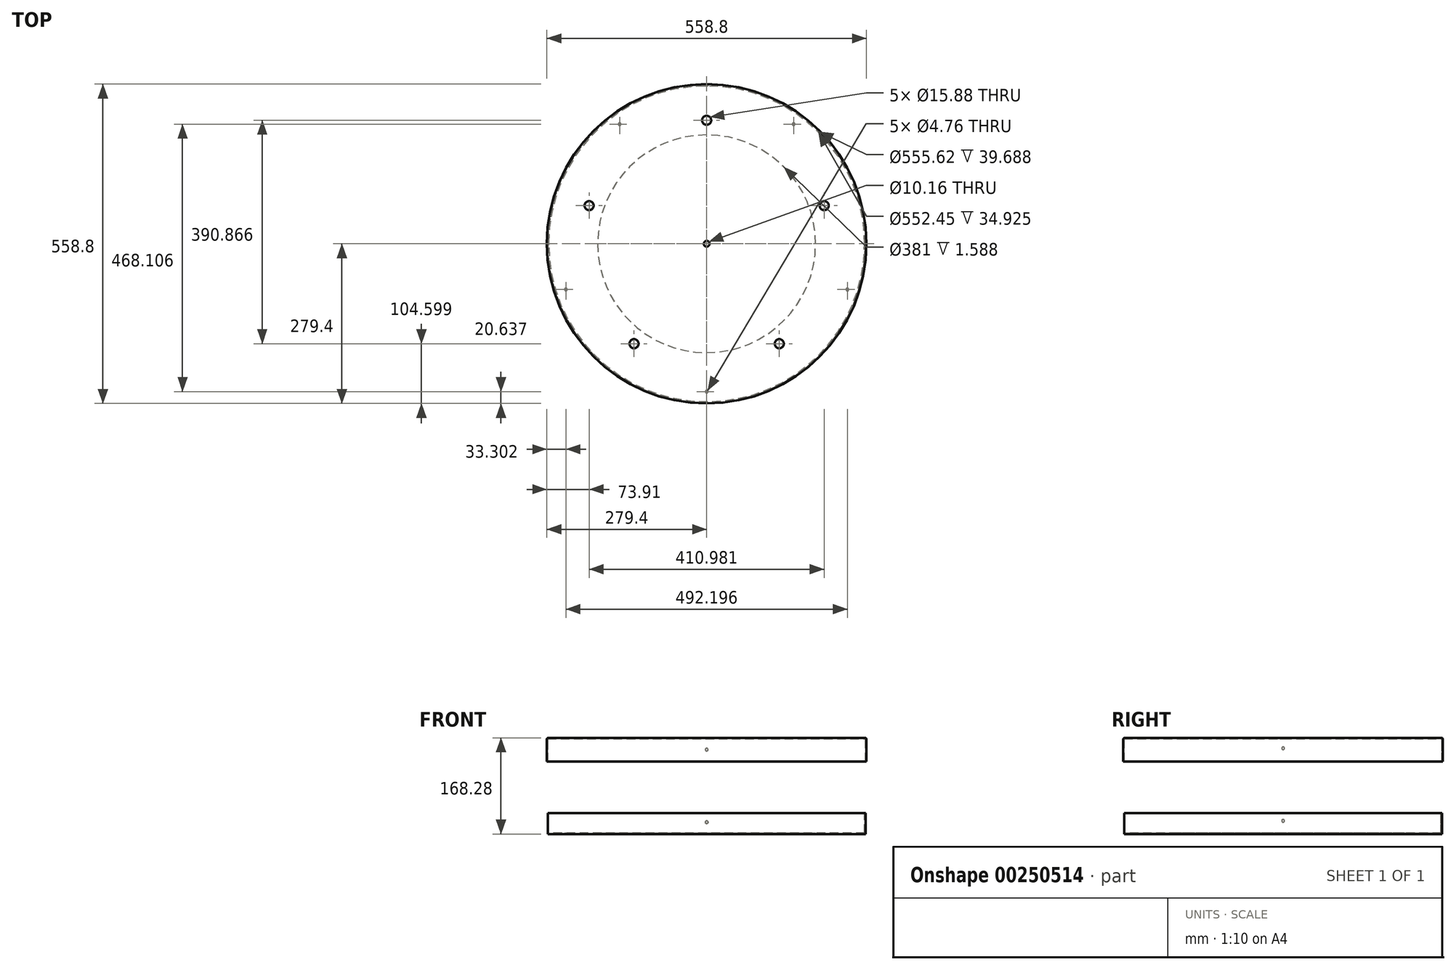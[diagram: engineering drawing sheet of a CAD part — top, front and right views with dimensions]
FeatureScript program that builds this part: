
annotation { "Feature Type Name" : "Feature", "Feature Type Description" : "" }
export const myFeature = defineFeature(function(context is Context, id is Id, definition is map)
    precondition{}
    {
        {
            var Q0;
            Q0=qCreatedBy(makeId("Top.planeOp"),FACE);
            var sketch = newSketch(context, id + "F0", { "sketchPlane" : qUnion([Q0])});
            skCircle(sketch, "E0", {"center": v(0, 0) * mm, "radius": 279.4 * mm});
            skSolve(sketch);
        }
        {
            var Q0;
            Q0 = qSketchRegion(id + "F0", true);
            extrude(context, id + "F1", {"entities" : qUnion([Q0]), "depth" : 1.59 * mm});
        }
        {
            var Q0;
            Q0=makeQuery(id+"F1.opExtrude","CAP_FACE",FACE,{"disambiguationData":[OSD([sQuery(id+"F0.wireOp",EDGE,"E0")])],"isStart":true});
            var sketch = newSketch(context, id + "F2", { "sketchPlane" : qUnion([Q0])});
            skCircle(sketch, "E1.0", {"center": v(0, 0) * mm, "radius": 279.4 * mm});
            skCircle(sketch, "E2.0", {"center": v(0, 0) * mm, "radius": 277.81 * mm});
            skSolve(sketch);
        }
        {
            var Q0;
            Q0 = qSketchRegion(id + "F2", true);
            extrude(context, id + "F3", {"entities" : qUnion([Q0]), "operationType" : NewBodyOperationType.ADD, "depth" : 39.69 * mm});
        }
        {
            var Q0;
            Q0=makeQuery(id+"F1.opExtrude","CAP_FACE",FACE,{"disambiguationData":[OSD([sQuery(id+"F0.wireOp",EDGE,"E0")])],"isStart":false});
            var sketch = newSketch(context, id + "F4", { "sketchPlane" : qUnion([Q0])});
            skCircle(sketch, "E3", {"center": v(0, 216.07) * mm, "radius": 7.94 * mm});
            skCircle(sketch, "E4.1.0", {"center": v(-205.5, 66.77) * mm, "radius": 7.94 * mm});
            skCircle(sketch, "E4.2.0", {"center": v(-127, -174.8) * mm, "radius": 7.94 * mm});
            skCircle(sketch, "E4.3.0", {"center": v(127, -174.8) * mm, "radius": 7.94 * mm});
            skCircle(sketch, "E4.4.0", {"center": v(205.5, 66.77) * mm, "radius": 7.94 * mm});
            skPoint(sketch, "E4.center", {"position": v(0, 0) * mm});
            skCircle(sketch, "E5", {"center": v(0, 0) * mm, "radius": 5.08 * mm});
            skSolve(sketch);
        }
        {
            var Q0;
            Q0 = qSketchRegion(id + "F4", true);
            var Q1;
            Q1=makeQuery(id+"F1.opExtrude","CAP_FACE",FACE,{"disambiguationData":[OSD([sQuery(id+"F0.wireOp",EDGE,"E0")])],"isStart":true});
            extrude(context, id + "F5", {"entities" : qUnion([Q0]), "operationType" : NewBodyOperationType.REMOVE, "endBound" : BoundingType.UP_TO_SURFACE, "oppositeDirection" : true, "endBoundEntityFace" : qUnion([Q1]), "depth" : 25.4 * mm});
        }
        {
            var Q0;
            Q0=makeQuery(id+"F1.opExtrude","CAP_EDGE",EDGE,{"disambiguationData":[OSD([sQuery(id+"F0.wireOp",EDGE,"E0")])],"isStart":false});
            fillet(context, id + "F6", {"entities" : qUnion([Q0]), "radius" : 2.54 * mm, "tangentPropagation" : true, "allowEdgeOverflow" : false});
        }
        {
            var Q0;
            Q0=qCreatedBy(makeId("Front.planeOp"),FACE);
            var sketch = newSketch(context, id + "F7", { "sketchPlane" : qUnion([Q0])});
            skLineSegment(sketch, "E6.0", {"start": v(277.81, 0) * mm, "end": v(-277.81, 0) * mm, "construction": true});
            skLineSegment(sketch, "E6.1", {"start": v(277.81, -39.69) * mm, "end": v(-277.81, -39.69) * mm, "construction": true});
            skLineSegment(sketch, "E7", {"start": v(277.81, -39.69) * mm, "end": v(277.81, -3.18) * mm});
            skLineSegment(sketch, "E8", {"start": v(277.81, -3.18) * mm, "end": v(276.23, -3.18) * mm});
            skLineSegment(sketch, "E9", {"start": v(276.23, -3.18) * mm, "end": v(276.23, -38.1) * mm});
            skLineSegment(sketch, "E10", {"start": v(276.23, -38.1) * mm, "end": v(0, -38.1) * mm});
            skLineSegment(sketch, "E11", {"start": v(0, -38.1) * mm, "end": v(0, -39.69) * mm});
            skLineSegment(sketch, "E12", {"start": v(0, -39.69) * mm, "end": v(277.81, -39.69) * mm});
            skLineSegment(sketch, "E13", {"start": v(0, -39.69) * mm, "end": v(0, -99.27) * mm, "construction": true});
            skSolve(sketch);
        }
        {
            var Q0;
            Q0 = qSketchRegion(id + "F7", true);
            var Q1;
            Q1=sQuery(id+"F7.wireOp",EDGE,"E13");
            revolve(context, id + "F8", {"entities" : qUnion([Q0]), "axis" : qUnion([Q1]), "revolveType" : RevolveType.FULL});
        }
        {
            var Q0;
            Q0=makeQuery(id+"F8.opRevolve","SWEPT_FACE",FACE,{"disambiguationData":[OSD([sQuery(id+"F7.wireOp",EDGE,"E12")])]});
            var sketch = newSketch(context, id + "F9", { "sketchPlane" : qUnion([Q0])});
            skCircle(sketch, "E14", {"center": v(0, 0) * mm, "radius": 190.5 * mm});
            skCircle(sketch, "E15", {"center": v(0, 258.76) * mm, "radius": 2.38 * mm});
            skCircle(sketch, "E16.1.0", {"center": v(-246.1, 79.96) * mm, "radius": 2.38 * mm});
            skCircle(sketch, "E16.2.0", {"center": v(-152.1, -209.34) * mm, "radius": 2.38 * mm});
            skCircle(sketch, "E16.3.0", {"center": v(152.1, -209.34) * mm, "radius": 2.38 * mm});
            skCircle(sketch, "E16.4.0", {"center": v(246.1, 79.96) * mm, "radius": 2.38 * mm});
            skSolve(sketch);
        }
        {
            var Q0;
            Q0 = qSketchRegion(id + "F9", true);
            extrude(context, id + "F10", {"entities" : qUnion([Q0]), "operationType" : NewBodyOperationType.REMOVE, "oppositeDirection" : true, "depth" : 3.17 * mm});
        }
        {
            var Q0;
            Q0=qCreatedBy(makeId("Front.planeOp"),FACE);
            var sketch = newSketch(context, id + "F11", { "sketchPlane" : qUnion([Q0])});
            skLineSegment(sketch, "E17", {"start": v(0, 0) * mm, "end": v(0, -110.02) * mm, "construction": true});
            skSolve(sketch);
        }
        {
            var Q0;
            Q0=qCreatedBy(makeId("Front.planeOp"),FACE);
            var sketch = newSketch(context, id + "F12", { "sketchPlane" : qUnion([Q0])});
            skCircle(sketch, "E18", {"center": v(0, -19.05) * mm, "radius": 2.38 * mm});
            skSolve(sketch);
        }
        {
            var Q0;
            Q0 = qSketchRegion(id + "F12", true);
            extrude(context, id + "F13", {"entities" : qUnion([Q0]), "operationType" : NewBodyOperationType.REMOVE, "endBound" : BoundingType.THROUGH_ALL, "oppositeDirection" : true, "depth" : 25.4 * mm});
        }
        {
            var Q0;
            Q0=qCreatedBy(makeId("Right.planeOp"),FACE);
            var sketch = newSketch(context, id + "F14", { "sketchPlane" : qUnion([Q0])});
            skFitSpline(sketch, "E19.0", {"points": [v(279.4, -21.43) * mm, v(279.4, -21.43) * mm, v(279.4, -21.34) * mm, v(279.4, -21.04) * mm, v(279.4, -20.74) * mm, v(279.4, -20.38) * mm, v(279.4, -20.04) * mm, v(279.4, -19.75) * mm, v(279.4, -19.44) * mm, v(279.39, -19.06) * mm, v(279.4, -18.58) * mm, v(279.4, -18.14) * mm, v(279.4, -17.72) * mm, v(279.4, -17.24) * mm, v(279.4, -16.8) * mm, v(279.4, -16.67) * mm, v(279.4, -16.67) * mm], "construction": true});
            skLineSegment(sketch, "E20", {"start": v(279.39, -19.02) * mm, "end": v(0, -16.67) * mm, "construction": true});
            skCircle(sketch, "E21", {"center": v(0, -16.67) * mm, "radius": 2.38 * mm});
            skSolve(sketch);
        }
        {
            var Q0;
            Q0 = qSketchRegion(id + "F14", true);
            extrude(context, id + "F15", {"entities" : qUnion([Q0]), "operationType" : NewBodyOperationType.REMOVE, "endBound" : BoundingType.THROUGH_ALL, "oppositeDirection" : true, "depth" : 25.4 * mm});
        }
        {
            var Q0;
            Q0=makeQuery(id+"F8.opRevolve","SWEPT_BODY",BODY,{"disambiguationData":[OSD([sQuery(id+"F7.wireOp",EDGE,"E7"),sQuery(id+"F7.wireOp",EDGE,"E8"),sQuery(id+"F7.wireOp",EDGE,"E9"),sQuery(id+"F7.wireOp",EDGE,"E10"),sQuery(id+"F7.wireOp",EDGE,"E11"),sQuery(id+"F7.wireOp",EDGE,"E12")])]});
            var Q1;
            Q1=sQuery(id+"F11.wireOp",EDGE,"E17");
            var Q2;
            Q2=sQuery(id+"F11.wireOp",EDGE,"E17");
            transform(context, id + "F16", {"entities" : qUnion([Q0]), "transformType" : TransformType.TRANSLATION_DISTANCE, "transformDirection" : qUnion([Q2]), "distance" : 127 * mm, "makeCopy" : false});
        }
    });
